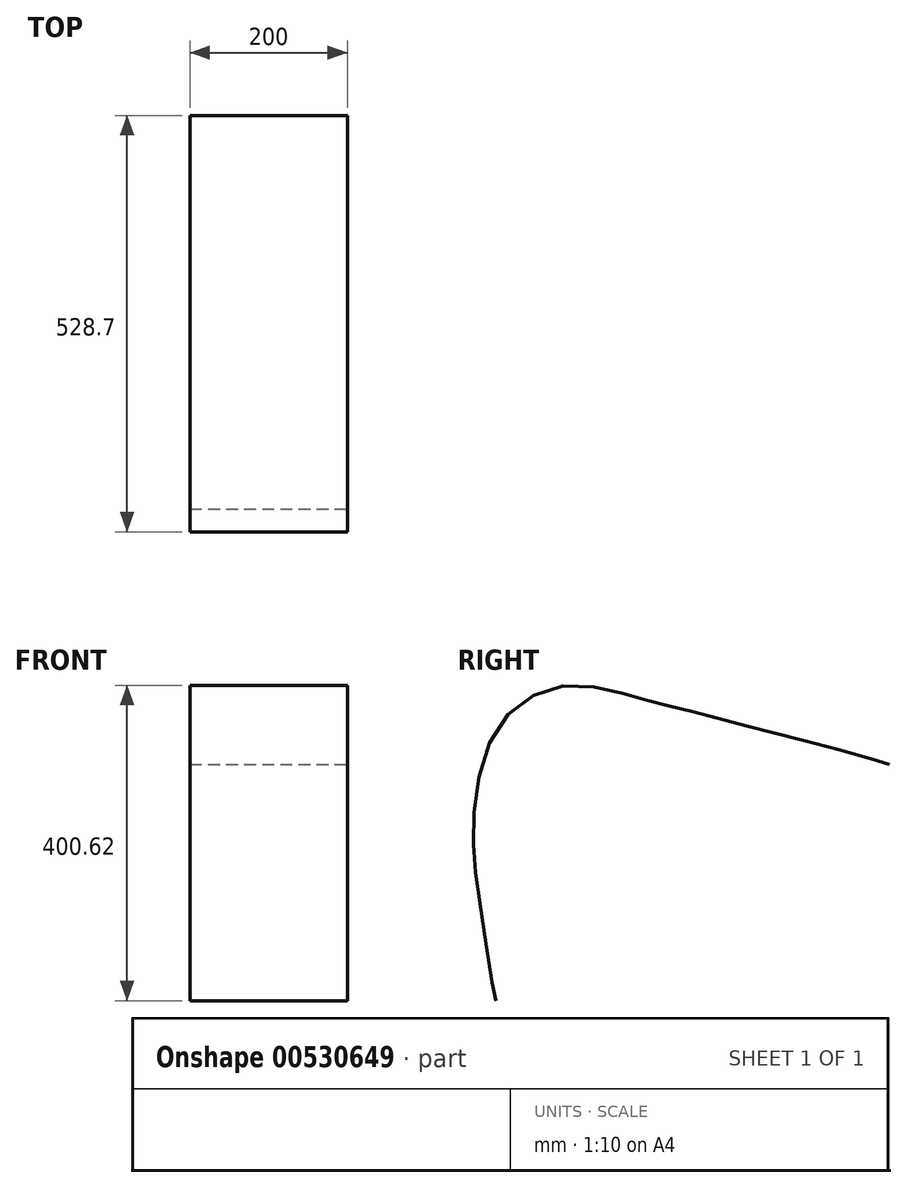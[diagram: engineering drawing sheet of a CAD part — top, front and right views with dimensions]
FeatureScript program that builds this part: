
annotation { "Feature Type Name" : "Feature", "Feature Type Description" : "" }
export const myFeature = defineFeature(function(context is Context, id is Id, definition is map)
    precondition{}
    {
        {
            var Q0;
            Q0=qCreatedBy(makeId("Right.planeOp"),FACE);
            var sketch = newSketch(context, id + "F0", { "sketchPlane" : qUnion([Q0])});
            skFitSpline(sketch, "E0", {"points": [v(0, 0) * mm, v(-18.92, 113.73) * mm, v(-28.67, 214.34) * mm, v(0, 343.62) * mm, v(87.8, 400) * mm, v(181.13, 384.55) * mm, v(234.14, 371.06) * mm, v(315.24, 349.71) * mm, v(412.81, 324.71) * mm, v(500, 300) * mm], "startDerivative": vector(-49, 67.02) * mm, "endDerivative": vector(152.42, -65.67) * mm});
            skSolve(sketch);
        }
        {
            var Q0;
            Q0=sQuery(id+"F0.wireOp",EDGE,"E0");
            extrude(context, id + "F1", {"bodyType" : ToolBodyType.SURFACE, "surfaceEntities" : qUnion([Q0]), "depth" : 200 * mm, "offsetDistance" : 25 * mm});
        }
    });
